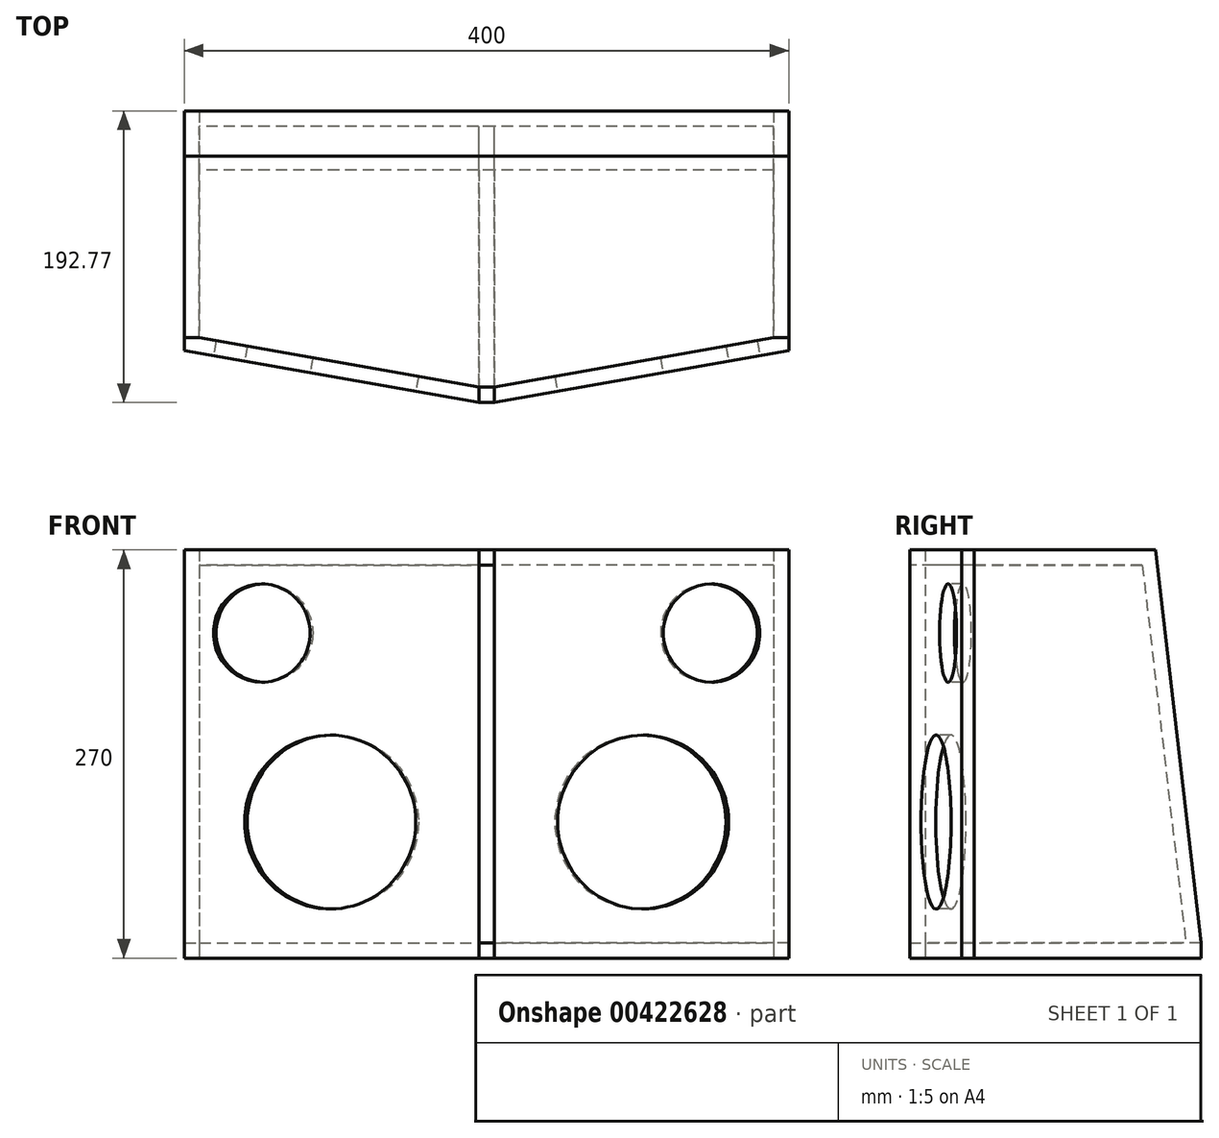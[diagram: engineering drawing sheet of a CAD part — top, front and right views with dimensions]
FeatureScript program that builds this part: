
annotation { "Feature Type Name" : "Feature", "Feature Type Description" : "" }
export const myFeature = defineFeature(function(context is Context, id is Id, definition is map)
    precondition{}
    {
        {
            var Q0;
            Q0=qCreatedBy(makeId("Top.planeOp"),FACE);
            var sketch = newSketch(context, id + "F0", { "sketchPlane" : qUnion([Q0])});
            skLineSegment(sketch, "E0", {"start": v(0, 0) * mm, "end": v(380, 0) * mm});
            skLineSegment(sketch, "E1", {"start": v(0, 0) * mm, "end": v(0, -150) * mm});
            skLineSegment(sketch, "E2", {"start": v(0, -150) * mm, "end": v(185, -182.62) * mm});
            skLineSegment(sketch, "E3", {"start": v(380, 0) * mm, "end": v(380, -150) * mm});
            skLineSegment(sketch, "E4", {"start": v(380, -150) * mm, "end": v(195, -182.62) * mm});
            skLineSegment(sketch, "E5", {"start": v(185, -182.62) * mm, "end": v(195, -182.62) * mm});
            skLineSegment(sketch, "E6", {"start": v(0, 0) * mm, "end": v(-10, 0) * mm});
            skLineSegment(sketch, "E7", {"start": v(-10, 0) * mm, "end": v(-10, -150) * mm});
            skLineSegment(sketch, "E8", {"start": v(-10, -150) * mm, "end": v(0, -150) * mm});
            skLineSegment(sketch, "E9", {"start": v(0, -10) * mm, "end": v(380, -10) * mm});
            skLineSegment(sketch, "E10", {"start": v(185, -182.62) * mm, "end": v(183.26, -192.47) * mm, "construction": true});
            skLineSegment(sketch, "E11", {"start": v(183.26, -192.47) * mm, "end": v(-11.43, -158.14) * mm, "construction": true});
            skLineSegment(sketch, "E12", {"start": v(-10, -150) * mm, "end": v(-10, -158.4) * mm});
            skLineSegment(sketch, "E13", {"start": v(-10, -158.4) * mm, "end": v(183.26, -192.47) * mm});
            skLineSegment(sketch, "E14", {"start": v(0, -150) * mm, "end": v(-9.7, -148.29) * mm, "construction": true});
            skLineSegment(sketch, "E15", {"start": v(-11.43, -158.14) * mm, "end": v(-9.7, -148.29) * mm, "construction": true});
            skLineSegment(sketch, "E16", {"start": v(183.26, -192.47) * mm, "end": v(185, -192.77) * mm, "construction": true});
            skLineSegment(sketch, "E17", {"start": v(185, -182.62) * mm, "end": v(185, -192.77) * mm});
            skLineSegment(sketch, "E18", {"start": v(185, -192.77) * mm, "end": v(186.74, -182.93) * mm, "construction": true});
            skLineSegment(sketch, "E19", {"start": v(185, -182.62) * mm, "end": v(186.74, -182.93) * mm, "construction": true});
            skLineSegment(sketch, "E20", {"start": v(190, -182.62) * mm, "end": v(190, -10) * mm, "construction": true});
            skLineSegment(sketch, "E21.MirrorCS", {"start": v(195, -192.77) * mm, "end": v(193.26, -182.93) * mm, "construction": true});
            skLineSegment(sketch, "E22.MirrorCS", {"start": v(195, -182.62) * mm, "end": v(193.26, -182.93) * mm, "construction": true});
            skLineSegment(sketch, "E23.MirrorCS", {"start": v(195, -182.62) * mm, "end": v(195, -192.77) * mm});
            skLineSegment(sketch, "E24.MirrorCS", {"start": v(196.74, -192.47) * mm, "end": v(195, -192.77) * mm, "construction": true});
            skLineSegment(sketch, "E25.MirrorCS", {"start": v(195, -182.62) * mm, "end": v(196.74, -192.47) * mm, "construction": true});
            skLineSegment(sketch, "E26.MirrorCS", {"start": v(196.74, -192.47) * mm, "end": v(391.43, -158.14) * mm, "construction": true});
            skLineSegment(sketch, "E27.MirrorCS", {"start": v(390, -150) * mm, "end": v(390, -158.4) * mm});
            skLineSegment(sketch, "E28.MirrorCS", {"start": v(391.43, -158.14) * mm, "end": v(389.7, -148.29) * mm, "construction": true});
            skLineSegment(sketch, "E29.MirrorCS", {"start": v(380, -150) * mm, "end": v(389.7, -148.29) * mm, "construction": true});
            skLineSegment(sketch, "E30", {"start": v(-10, -158.4) * mm, "end": v(185, -192.77) * mm});
            skLineSegment(sketch, "E31", {"start": v(185, -192.77) * mm, "end": v(195, -192.77) * mm});
            skLineSegment(sketch, "E32", {"start": v(195, -182.62) * mm, "end": v(195, -62.62) * mm});
            skLineSegment(sketch, "E33", {"start": v(195, -62.62) * mm, "end": v(185, -62.62) * mm});
            skLineSegment(sketch, "E34", {"start": v(185, -62.62) * mm, "end": v(185, -182.62) * mm});
            skLineSegment(sketch, "E35", {"start": v(380, 0) * mm, "end": v(390, 0) * mm});
            skLineSegment(sketch, "E36", {"start": v(390, 0) * mm, "end": v(390, -150) * mm});
            skLineSegment(sketch, "E37", {"start": v(380, -150) * mm, "end": v(390, -150) * mm});
            skLineSegment(sketch, "E38", {"start": v(195, -192.77) * mm, "end": v(390, -158.4) * mm});
            skSolve(sketch);
        }
        {
            var Q0;
            {var subQ3=sQuery(id+"F0.wireOp",EDGE,"E2");Q0=makeQuery(id+"F0.imprint","IMPRINT",FACE,{"disambiguationData":[TD([[makeQuery(id+"F0.imprint","IMPRINT",EDGE,{"derivedFrom":subQ3}),1.0]])]});}
            var Q1;
            Q1=makeQuery(id+"F0.imprint","IMPRINT",FACE,{"disambiguationData":[TD([[makeQuery(id+"F0.imprint","IMPRINT",EDGE,{"derivedFrom":sQuery(id+"F0.wireOp",EDGE,"E5")}),1.0]])]});
            var Q2;
            {var subQ0=sQuery(id+"F0.wireOp",EDGE,"E0");Q2=makeQuery(id+"F0.imprint","IMPRINT",FACE,{"disambiguationData":[TD([[makeQuery(id+"F0.imprint","IMPRINT",EDGE,{"derivedFrom":subQ0}),-1.0]])]});}
            extrude(context, id + "F1", {"entities" : qUnion([Q0, Q1, Q2]), "depth" : 10 * mm});
        }
        {
            var Q0;
            Q0=makeQuery(id+"F0.imprint","IMPRINT",FACE,{"disambiguationData":[TD([[makeQuery(id+"F0.imprint","IMPRINT",EDGE,{"derivedFrom":sQuery(id+"F0.wireOp",EDGE,"E2")}),-1.0]])]});
            extrude(context, id + "F2", {"entities" : qUnion([Q0]), "depth" : 270 * mm});
        }
        {
            var Q0;
            Q0=makeQuery(id+"F0.imprint","IMPRINT",FACE,{"disambiguationData":[TD([[makeQuery(id+"F0.imprint","IMPRINT",EDGE,{"derivedFrom":sQuery(id+"F0.wireOp",EDGE,"E4")}),1.0]])]});
            extrude(context, id + "F3", {"entities" : qUnion([Q0]), "depth" : 270 * mm});
        }
        {
            var Q0;
            Q0=makeQuery(id+"F1.opExtrude","CAP_FACE",FACE,{"disambiguationData":[OSD([sQuery(id+"F0.wireOp",EDGE,"E1"),sQuery(id+"F0.wireOp",EDGE,"E2"),sQuery(id+"F0.wireOp",EDGE,"E3"),sQuery(id+"F0.wireOp",EDGE,"E4"),sQuery(id+"F0.wireOp",EDGE,"E5"),sQuery(id+"F0.wireOp",EDGE,"E9")])],"isStart":false});
            cPlane(context, id + "F4", {"entities" : qUnion([Q0]), "cplaneType" : CPlaneType.OFFSET, "offset" : 250 * mm, "width" : 150 * mm, "height" : 150 * mm});
        }
        {
            var Q0;
            Q0=qCreatedBy(id+"F4.planeOp",FACE);
            var sketch = newSketch(context, id + "F5", { "sketchPlane" : qUnion([Q0])});
            skLineSegment(sketch, "E39.0", {"start": v(380, -150) * mm, "end": v(390, -150) * mm});
            skLineSegment(sketch, "E40.0", {"start": v(380, -150) * mm, "end": v(195, -182.62) * mm});
            skLineSegment(sketch, "E41.0", {"start": v(-10, -150) * mm, "end": v(0, -150) * mm});
            skLineSegment(sketch, "E42.0", {"start": v(0, -150) * mm, "end": v(185, -182.62) * mm});
            skLineSegment(sketch, "E43", {"start": v(0, -150) * mm, "end": v(0, -30) * mm});
            skLineSegment(sketch, "E44", {"start": v(0, -30) * mm, "end": v(-10, -30) * mm});
            skLineSegment(sketch, "E45", {"start": v(-10, -30) * mm, "end": v(-10, -150) * mm});
            skLineSegment(sketch, "E46", {"start": v(380, -150) * mm, "end": v(380, -30) * mm});
            skLineSegment(sketch, "E47", {"start": v(380, -30) * mm, "end": v(390, -30) * mm});
            skLineSegment(sketch, "E48", {"start": v(390, -30) * mm, "end": v(390, -150) * mm});
            skLineSegment(sketch, "E49", {"start": v(0, -30) * mm, "end": v(380, -30) * mm});
            skLineSegment(sketch, "E50", {"start": v(185, -182.62) * mm, "end": v(195, -182.62) * mm});
            skSolve(sketch);
        }
        {
            var Q0;
            Q0=makeQuery(id+"F1.opExtrude","SWEPT_FACE",FACE,{"disambiguationData":[OSD([sQuery(id+"F0.wireOp",EDGE,"E1")])]});
            var sketch = newSketch(context, id + "F6", { "sketchPlane" : qUnion([Q0])});
            skLineSegment(sketch, "E51", {"start": v(0, 0) * mm, "end": v(150, 0) * mm});
            skLineSegment(sketch, "E52", {"start": v(150, 0) * mm, "end": v(150, 270) * mm});
            skLineSegment(sketch, "E53", {"start": v(0, 10) * mm, "end": v(0, 0) * mm});
            skLineSegment(sketch, "E54", {"start": v(150, 270) * mm, "end": v(30, 270) * mm});
            skLineSegment(sketch, "E55", {"start": v(30, 270) * mm, "end": v(0, 10) * mm});
            skSolve(sketch);
        }
        {
            var Q0;
            {var subQ0=sQuery(id+"F6.wireOp",EDGE,"E53");Q0=makeQuery(id+"F6.imprint","IMPRINT",FACE,{"disambiguationData":[TD([[makeQuery(id+"F6.imprint","IMPRINT",EDGE,{"derivedFrom":subQ0}),1.0]])]});}
            var Q1;
            {var subQ3=sQuery(id+"F0.wireOp",EDGE,"E1");var subQ5=makeQuery(id+"F1.opExtrude","CAP_EDGE",EDGE,{"disambiguationData":[OSD([subQ3])],"isStart":false});Q1=makeQuery(id+"F6.imprint","IMPRINT",FACE,{"disambiguationData":[TD([[makeQuery(id+"F6.imprint","IMPRINT",EDGE,{"derivedFrom":subQ5}),-1.0]])]});}
            var Q2;
            {var subQ2=sQuery(id+"F6.wireOp",EDGE,"E54");Q2=makeQuery(id+"F6.imprint","IMPRINT",FACE,{"disambiguationData":[TD([[makeQuery(id+"F6.imprint","IMPRINT",EDGE,{"derivedFrom":subQ2}),1.0]])]});}
            extrude(context, id + "F7", {"entities" : qUnion([Q0, Q1, Q2]), "depth" : 10 * mm});
        }
        {
            var Q0;
            Q0=makeQuery(id+"F1.opExtrude","SWEPT_FACE",FACE,{"disambiguationData":[OSD([sQuery(id+"F0.wireOp",EDGE,"E3")])]});
            var sketch = newSketch(context, id + "F8", { "sketchPlane" : qUnion([Q0])});
            skLineSegment(sketch, "E56", {"start": v(-150, 0) * mm, "end": v(0, 0) * mm});
            skLineSegment(sketch, "E57", {"start": v(0, 0) * mm, "end": v(0, 10) * mm});
            skLineSegment(sketch, "E58", {"start": v(0, 10) * mm, "end": v(-30, 270) * mm});
            skLineSegment(sketch, "E59", {"start": v(-30, 270) * mm, "end": v(-150, 270) * mm});
            skLineSegment(sketch, "E60", {"start": v(-150, 270) * mm, "end": v(-150, 0) * mm});
            skSolve(sketch);
        }
        {
            var Q0;
            {var subQ1=sQuery(id+"F8.wireOp",EDGE,"E57");Q0=makeQuery(id+"F8.imprint","IMPRINT",FACE,{"disambiguationData":[TD([[makeQuery(id+"F8.imprint","IMPRINT",EDGE,{"derivedFrom":subQ1}),1.0]])]});}
            var Q1;
            {var subQ3=sQuery(id+"F0.wireOp",EDGE,"E3");var subQ5=makeQuery(id+"F1.opExtrude","CAP_EDGE",EDGE,{"disambiguationData":[OSD([subQ3])],"isStart":false});Q1=makeQuery(id+"F8.imprint","IMPRINT",FACE,{"disambiguationData":[TD([[makeQuery(id+"F8.imprint","IMPRINT",EDGE,{"derivedFrom":subQ5}),1.0]])]});}
            var Q2;
            Q2=makeQuery(id+"F8.imprint","IMPRINT",FACE,{"disambiguationData":[TD([[makeQuery(id+"F8.imprint","IMPRINT",EDGE,{"derivedFrom":sQuery(id+"F8.wireOp",EDGE,"E58")}),1.0]])]});
            extrude(context, id + "F9", {"entities" : qUnion([Q0, Q1, Q2]), "depth" : 10 * mm});
        }
        {
            var Q0;
            Q0=makeQuery(id+"F7.opExtrude","CAP_FACE",FACE,{"disambiguationData":[OSD([sQuery(id+"F6.wireOp",EDGE,"E51"),sQuery(id+"F6.wireOp",EDGE,"E52"),sQuery(id+"F6.wireOp",EDGE,"E53"),sQuery(id+"F6.wireOp",EDGE,"E54"),sQuery(id+"F6.wireOp",EDGE,"E55")])],"isStart":true});
            var sketch = newSketch(context, id + "F10", { "sketchPlane" : qUnion([Q0])});
            skLineSegment(sketch, "E61", {"start": v(-28.85, 260) * mm, "end": v(0, 10) * mm});
            skLineSegment(sketch, "E62", {"start": v(-38.91, 260) * mm, "end": v(-10.07, 10) * mm});
            skLineSegment(sketch, "E63", {"start": v(0, 10) * mm, "end": v(-10.07, 10) * mm});
            skLineSegment(sketch, "E64", {"start": v(-28.85, 260) * mm, "end": v(-38.91, 260) * mm, "construction": true});
            skLineSegment(sketch, "E65", {"start": v(-38.91, 260) * mm, "end": v(-28.85, 260) * mm});
            skSolve(sketch);
        }
        {
            var Q0;
            Q0=makeQuery(id+"F10.imprint","IMPRINT",FACE,{"disambiguationData":[TD([[makeQuery(id+"F10.imprint","IMPRINT",EDGE,{"derivedFrom":sQuery(id+"F10.wireOp",EDGE,"E61")}),-1.0]])]});
            extrude(context, id + "F11", {"entities" : qUnion([Q0]), "depth" : 380 * mm});
        }
        {
            var Q0;
            {var subQ3=sQuery(id+"F5.wireOp",EDGE,"E40.0");Q0=makeQuery(id+"F5.imprint","IMPRINT",FACE,{"disambiguationData":[TD([[makeQuery(id+"F5.imprint","IMPRINT",EDGE,{"derivedFrom":subQ3}),-1.0]])]});}
            var Q1;
            {var subQ2=sQuery(id+"F5.wireOp",EDGE,"1eKeupN5-cQu7-t1ry-SB6c-v52Yv0l3lp1T");Q1=makeQuery(id+"F5.imprint","IMPRINT",FACE,{"disambiguationData":[TD([[makeQuery(id+"F5.imprint","IMPRINT",EDGE,{"derivedFrom":subQ2}),-1.0]])]});}
            extrude(context, id + "F12", {"entities" : qUnion([Q0, Q1]), "depth" : 10 * mm});
        }
        {
            var Q0;
            Q0=makeQuery(id+"F2.opExtrude","SWEPT_FACE",FACE,{"disambiguationData":[OSD([sQuery(id+"F0.wireOp",EDGE,"E30")])]});
            var sketch = newSketch(context, id + "F13", { "sketchPlane" : qUnion([Q0])});
            skCircle(sketch, "E66", {"center": v(115.66, 90) * mm, "radius": 79 * mm});
            skCircle(sketch, "E67", {"center": v(69.66, 215) * mm, "radius": 45.5 * mm});
            skCircle(sketch, "E68", {"center": v(115.66, 90) * mm, "radius": 57.5 * mm});
            skCircle(sketch, "E69", {"center": v(69.66, 215) * mm, "radius": 32.5 * mm});
            skSolve(sketch);
        }
        {
            var Q0;
            Q0=makeQuery(id+"F13.imprint","IMPRINT",FACE,{"disambiguationData":[TD([[makeQuery(id+"F13.imprint","IMPRINT",EDGE,{"derivedFrom":sQuery(id+"F13.wireOp",EDGE,"E69")}),1.0]])]});
            var Q1;
            Q1=makeQuery(id+"F13.imprint","IMPRINT",FACE,{"disambiguationData":[TD([[makeQuery(id+"F13.imprint","IMPRINT",EDGE,{"derivedFrom":sQuery(id+"F13.wireOp",EDGE,"E68")}),1.0]])]});
            extrude(context, id + "F14", {"entities" : qUnion([Q0, Q1]), "operationType" : NewBodyOperationType.REMOVE, "oppositeDirection" : true, "depth" : 25 * mm});
        }
        {
            var Q0;
            Q0=makeQuery(id+"F3.opExtrude","SWEPT_FACE",FACE,{"disambiguationData":[OSD([sQuery(id+"F0.wireOp",EDGE,"E38")])]});
            var sketch = newSketch(context, id + "F15", { "sketchPlane" : qUnion([Q0])});
            skCircle(sketch, "E70", {"center": v(258.57, 90) * mm, "radius": 79 * mm});
            skCircle(sketch, "E71", {"center": v(304.57, 215) * mm, "radius": 45.5 * mm});
            skCircle(sketch, "E72", {"center": v(304.57, 215) * mm, "radius": 32.5 * mm});
            skCircle(sketch, "E73", {"center": v(258.57, 90) * mm, "radius": 57.5 * mm});
            skSolve(sketch);
        }
        {
            var Q0;
            Q0=makeQuery(id+"F15.imprint","IMPRINT",FACE,{"disambiguationData":[TD([[makeQuery(id+"F15.imprint","IMPRINT",EDGE,{"derivedFrom":sQuery(id+"F15.wireOp",EDGE,"E73")}),1.0]])]});
            var Q1;
            Q1=makeQuery(id+"F15.imprint","IMPRINT",FACE,{"disambiguationData":[TD([[makeQuery(id+"F15.imprint","IMPRINT",EDGE,{"derivedFrom":sQuery(id+"F15.wireOp",EDGE,"E72")}),1.0]])]});
            extrude(context, id + "F16", {"entities" : qUnion([Q0, Q1]), "operationType" : NewBodyOperationType.REMOVE, "oppositeDirection" : true, "depth" : 25 * mm});
        }
        {
            var Q0;
            Q0=makeQuery(id+"F2.opExtrude","SWEPT_FACE",FACE,{"disambiguationData":[OSD([sQuery(id+"F0.wireOp",EDGE,"E17")])]});
            var sketch = newSketch(context, id + "F17", { "sketchPlane" : qUnion([Q0])});
            skLineSegment(sketch, "E74.0", {"start": v(-38.91, 260) * mm, "end": v(-10.07, 10) * mm});
            skLineSegment(sketch, "E75.0", {"start": v(-10.07, 10) * mm, "end": v(-150, 10) * mm});
            skLineSegment(sketch, "E76.0", {"start": v(-150, 10) * mm, "end": v(-182.62, 10) * mm});
            skLineSegment(sketch, "E77.0", {"start": v(-182.62, 260) * mm, "end": v(-182.62, 10) * mm});
            skPoint(sketch, "E78.orphan", {"position": v(-182.62, 270) * mm});
            skPoint(sketch, "E79.orphan", {"position": v(-30, 260) * mm});
            skPoint(sketch, "E80.orphan", {"position": v(0, 10) * mm});
            skPoint(sketch, "E81.orphan", {"position": v(-182.62, 0) * mm});
            skLineSegment(sketch, "E82", {"start": v(-182.62, 260) * mm, "end": v(-192.77, 260) * mm});
            skLineSegment(sketch, "E83", {"start": v(-192.77, 260) * mm, "end": v(-192.77, 10) * mm});
            skLineSegment(sketch, "E84", {"start": v(-192.77, 10) * mm, "end": v(-182.62, 10) * mm});
            skLineSegment(sketch, "E85", {"start": v(-182.62, 260) * mm, "end": v(-38.91, 260) * mm});
            skSolve(sketch);
        }
        {
            var Q0;
            Q0=makeQuery(id+"F17.imprint","IMPRINT",FACE,{"disambiguationData":[TD([[makeQuery(id+"F17.imprint","IMPRINT",EDGE,{"derivedFrom":sQuery(id+"F17.wireOp",EDGE,"dfc396f2-6645-452f-a475-9fc99da6a55c.0")}),1.0]])]});
            var Q1;
            Q1=makeQuery(id+"F17.imprint","IMPRINT",FACE,{"disambiguationData":[TD([[makeQuery(id+"F17.imprint","IMPRINT",EDGE,{"derivedFrom":sQuery(id+"F17.wireOp",EDGE,"E77.0")}),-1.0]])]});
            var Q2;
            Q2=makeQuery(id+"F17.imprint","IMPRINT",FACE,{"disambiguationData":[TD([[makeQuery(id+"F17.imprint","IMPRINT",EDGE,{"derivedFrom":sQuery(id+"F17.wireOp",EDGE,"E74.0")}),-1.0]])]});
            extrude(context, id + "F18", {"entities" : qUnion([Q0, Q1, Q2]), "depth" : 10 * mm});
        }
        {
            var Q0;
            Q0=makeQuery(id+"F9.opExtrude","CAP_FACE",FACE,{"disambiguationData":[OSD([sQuery(id+"F8.wireOp",EDGE,"E56"),sQuery(id+"F8.wireOp",EDGE,"E57"),sQuery(id+"F8.wireOp",EDGE,"E58"),sQuery(id+"F8.wireOp",EDGE,"E59"),sQuery(id+"F8.wireOp",EDGE,"E60")])],"isStart":true});
            var sketch = newSketch(context, id + "F19", { "sketchPlane" : qUnion([Q0])});
            skLineSegment(sketch, "E86", {"start": v(30, 270) * mm, "end": v(30, 260) * mm});
            skLineSegment(sketch, "E87", {"start": v(30, 260) * mm, "end": v(28.85, 260) * mm});
            skLineSegment(sketch, "E88", {"start": v(28.85, 260) * mm, "end": v(30, 270) * mm});
            skSolve(sketch);
        }
        {
            var Q0;
            Q0=makeQuery(id+"F19.imprint","IMPRINT",FACE,{"disambiguationData":[TD([[makeQuery(id+"F19.imprint","IMPRINT",EDGE,{"derivedFrom":sQuery(id+"F19.wireOp",EDGE,"E86")}),-1.0]])]});
            extrude(context, id + "F20", {"entities" : qUnion([Q0]), "operationType" : NewBodyOperationType.ADD, "depth" : 380 * mm});
        }
    });
